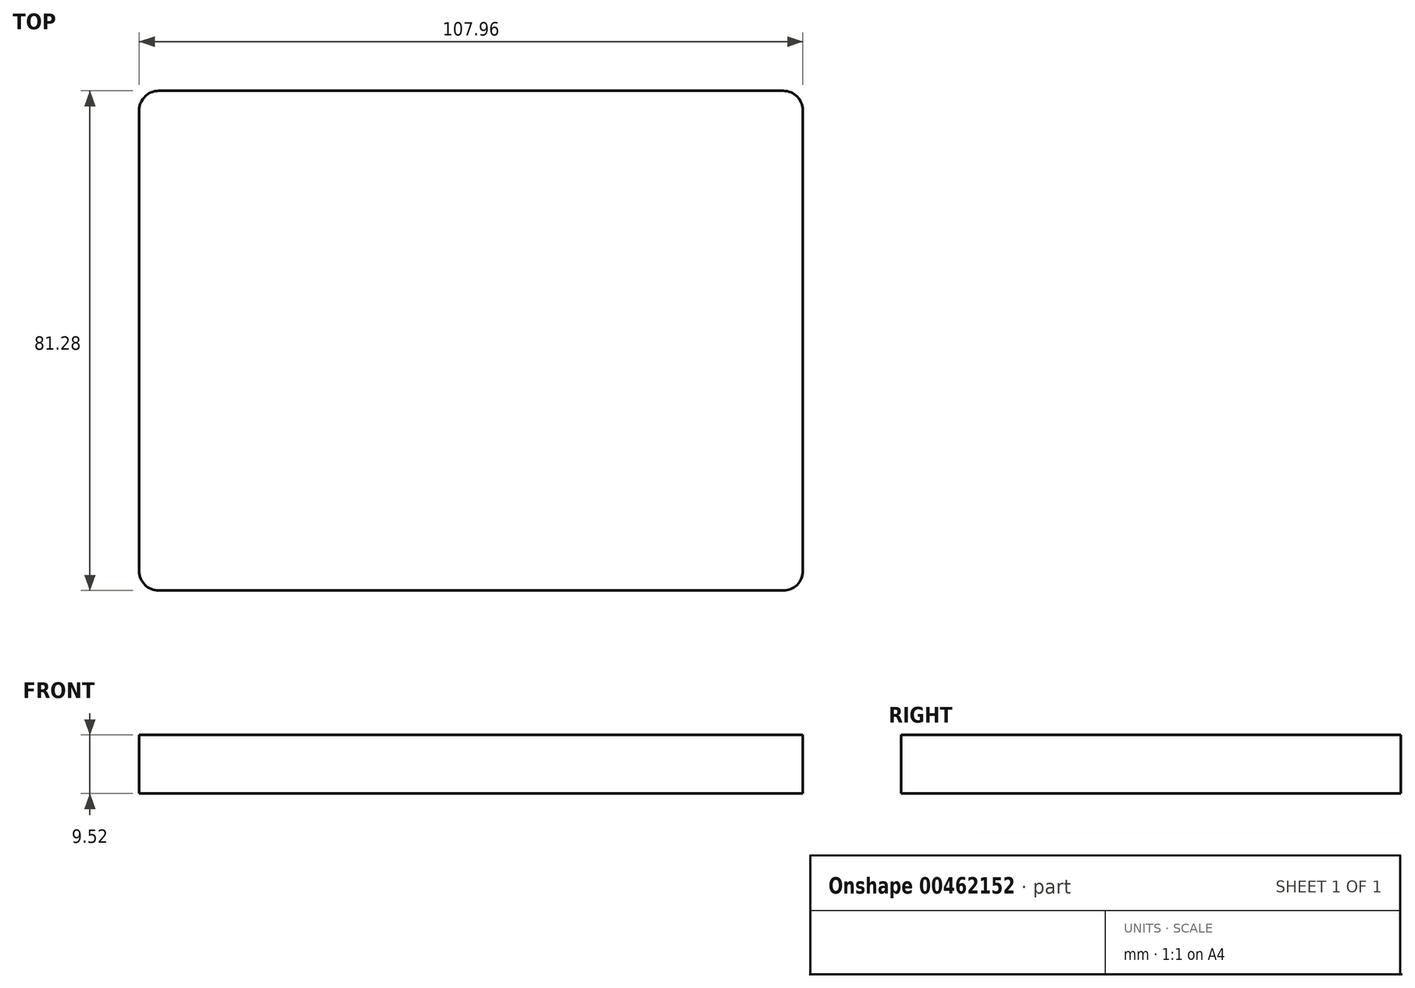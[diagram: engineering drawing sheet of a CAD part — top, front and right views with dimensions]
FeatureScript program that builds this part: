
annotation { "Feature Type Name" : "Feature", "Feature Type Description" : "" }
export const myFeature = defineFeature(function(context is Context, id is Id, definition is map)
    precondition{}
    {
        {
            var Q0;
            Q0=qCreatedBy(makeId("Top.planeOp"),FACE);
            var sketch = newSketch(context, id + "F0", { "sketchPlane" : qUnion([Q0])});
            skLineSegment(sketch, "E0.bottom", {"start": v(53.97, -40.64) * mm, "end": v(-53.98, -40.64) * mm});
            skLineSegment(sketch, "E0.top", {"start": v(53.98, 40.64) * mm, "end": v(-53.98, 40.64) * mm});
            skLineSegment(sketch, "E0.left", {"start": v(53.97, -40.64) * mm, "end": v(53.98, 40.64) * mm});
            skLineSegment(sketch, "E0.right", {"start": v(-53.98, -40.64) * mm, "end": v(-53.98, 40.64) * mm});
            skPoint(sketch, "E0.middle", {"position": v(0, 0) * mm});
            skSolve(sketch);
        }
        {
            var Q0;
            Q0=makeQuery(id+"F0.imprint","IMPRINT",FACE,{"disambiguationData":[TD([[makeQuery(id+"F0.imprint","IMPRINT",EDGE,{"derivedFrom":sQuery(id+"F0.wireOp",EDGE,"E0.bottom")}),-1.0]])]});
            extrude(context, id + "F1", {"entities" : qUnion([Q0]), "depth" : 9.52 * mm, "symmetric" : true});
        }
        {
            var Q0;
            Q0=makeQuery(id+"F1.opExtrude","SWEPT_EDGE",EDGE,{"disambiguationData":[OSD([sQuery(id+"F0.wireOp",EDGE,"E0.bottom"),sQuery(id+"F0.wireOp",EDGE,"E0.left")])]});
            var Q1;
            Q1=makeQuery(id+"F1.opExtrude","SWEPT_EDGE",EDGE,{"disambiguationData":[OSD([sQuery(id+"F0.wireOp",EDGE,"E0.top"),sQuery(id+"F0.wireOp",EDGE,"E0.left")])]});
            var Q2;
            Q2=makeQuery(id+"F1.opExtrude","SWEPT_EDGE",EDGE,{"disambiguationData":[OSD([sQuery(id+"F0.wireOp",EDGE,"E0.bottom"),sQuery(id+"F0.wireOp",EDGE,"E0.right")])]});
            var Q3;
            Q3=makeQuery(id+"F1.opExtrude","SWEPT_EDGE",EDGE,{"disambiguationData":[OSD([sQuery(id+"F0.wireOp",EDGE,"E0.top"),sQuery(id+"F0.wireOp",EDGE,"E0.right")])]});
            fillet(context, id + "F2", {"entities" : qUnion([Q0, Q1, Q2, Q3]), "radius" : 3.17 * mm, "tangentPropagation" : true, "allowEdgeOverflow" : false});
        }
    });
